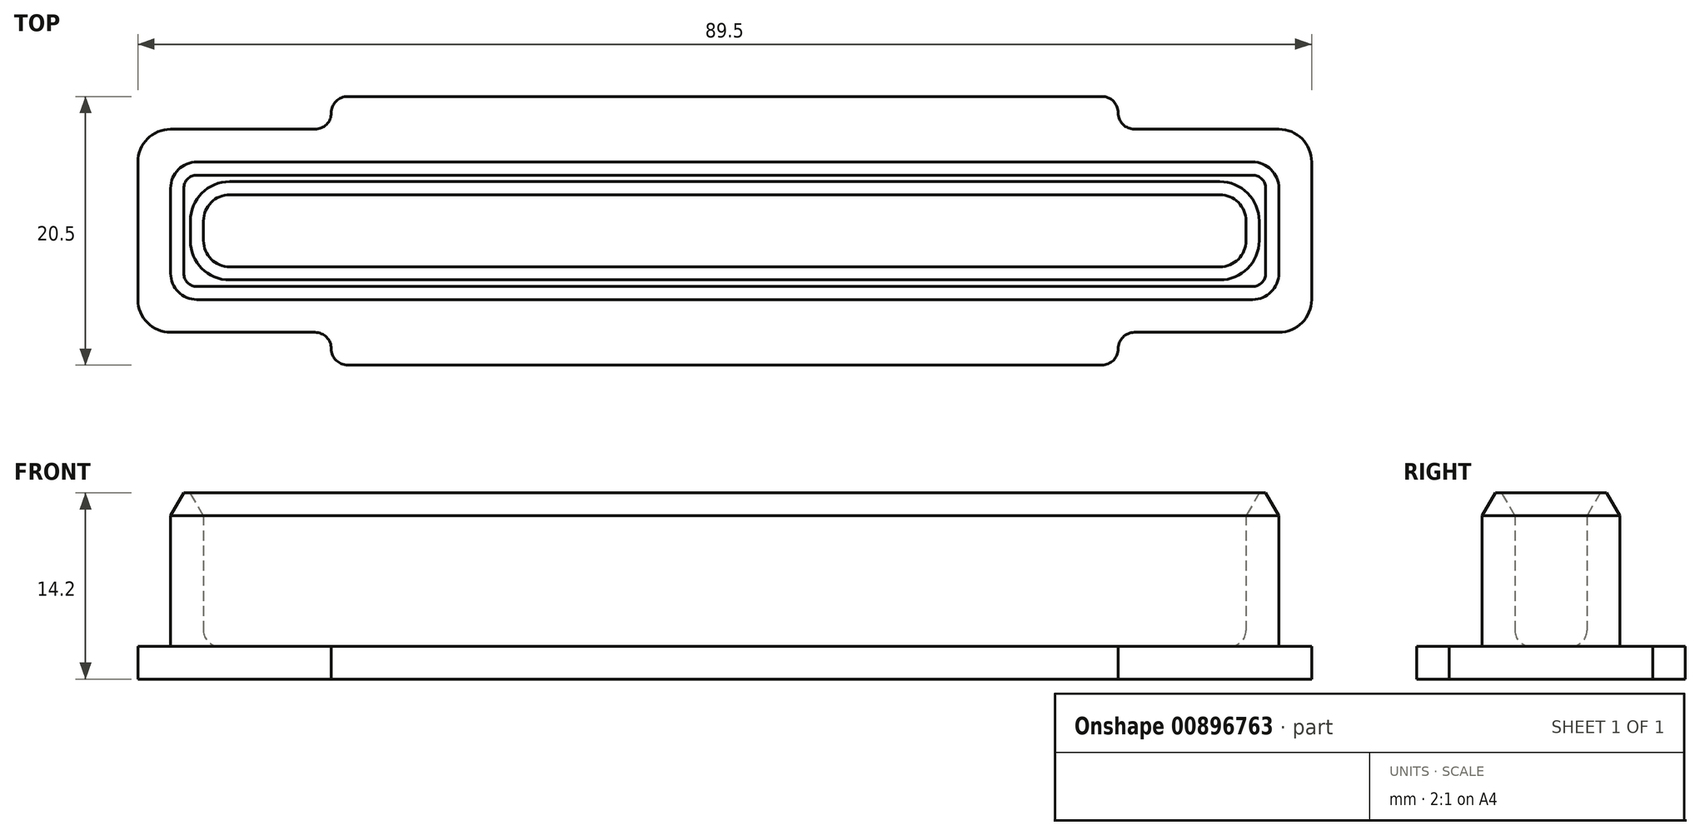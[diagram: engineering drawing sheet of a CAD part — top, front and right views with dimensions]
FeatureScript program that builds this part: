
annotation { "Feature Type Name" : "Feature", "Feature Type Description" : "" }
export const myFeature = defineFeature(function(context is Context, id is Id, definition is map)
    precondition{}
    {
        {
            var Q0;
            Q0=qCreatedBy(makeId("Top.planeOp"),FACE);
            var sketch = newSketch(context, id + "F0", { "sketchPlane" : qUnion([Q0])});
            skLineSegment(sketch, "E0.bottom", {"start": v(42.25, 5.25) * mm, "end": v(-42.25, 5.25) * mm});
            skLineSegment(sketch, "E0.top", {"start": v(42.25, -5.25) * mm, "end": v(-42.25, -5.25) * mm});
            skLineSegment(sketch, "E0.left", {"start": v(42.25, 5.25) * mm, "end": v(42.25, -5.25) * mm});
            skLineSegment(sketch, "E0.right", {"start": v(-42.25, 5.25) * mm, "end": v(-42.25, -5.25) * mm});
            skPoint(sketch, "E0.middle", {"position": v(0, 0) * mm});
            skLineSegment(sketch, "E1.bottom", {"start": v(44.75, 7.75) * mm, "end": v(-44.75, 7.75) * mm});
            skLineSegment(sketch, "E1.top", {"start": v(44.75, -7.75) * mm, "end": v(-44.75, -7.75) * mm});
            skLineSegment(sketch, "E1.left", {"start": v(44.75, 7.75) * mm, "end": v(44.75, -7.75) * mm});
            skLineSegment(sketch, "E1.right", {"start": v(-44.75, 7.75) * mm, "end": v(-44.75, -7.75) * mm});
            skLineSegment(sketch, "E2", {"start": v(0, 7.75) * mm, "end": v(0, 15.45) * mm, "construction": true});
            skLineSegment(sketch, "E3", {"start": v(0, 10.25) * mm, "end": v(30, 10.25) * mm});
            skLineSegment(sketch, "E4", {"start": v(30, 10.25) * mm, "end": v(30, 7.75) * mm});
            skLineSegment(sketch, "E5.MirrorCS", {"start": v(0, 10.25) * mm, "end": v(-30, 10.25) * mm});
            skLineSegment(sketch, "E6.MirrorCS", {"start": v(-30, 10.25) * mm, "end": v(-30, 7.75) * mm});
            skLineSegment(sketch, "E7.MirrorCS", {"start": v(0, -10.25) * mm, "end": v(30, -10.25) * mm});
            skLineSegment(sketch, "E8.MirrorCS", {"start": v(0, -10.25) * mm, "end": v(-30, -10.25) * mm});
            skLineSegment(sketch, "E9.MirrorCS", {"start": v(-30, -10.25) * mm, "end": v(-30, -7.75) * mm});
            skLineSegment(sketch, "E10.MirrorCS", {"start": v(30, -10.25) * mm, "end": v(30, -7.75) * mm});
            skSolve(sketch);
        }
        {
            var Q0;
            Q0=makeQuery(id+"F0.imprint","IMPRINT",FACE,{"disambiguationData":[TD([[makeQuery(id+"F0.imprint","IMPRINT",EDGE,{"derivedFrom":sQuery(id+"F0.wireOp",EDGE,"E0.bottom")}),1.0]])]});
            extrude(context, id + "F1", {"entities" : qUnion([Q0]), "depth" : 11.7 * mm, "offsetDistance" : 25 * mm});
        }
        {
            var Q0;
            Q0=makeQuery(id+"F1.opExtrude","CAP_FACE",FACE,{"disambiguationData":[OSD([sQuery(id+"F0.wireOp",EDGE,"E0.bottom"),sQuery(id+"F0.wireOp",EDGE,"E0.top"),sQuery(id+"F0.wireOp",EDGE,"E0.left"),sQuery(id+"F0.wireOp",EDGE,"E0.right")])],"isStart":false});
            var Q1;
            Q1=makeQuery(id+"F1.opExtrude","CAP_FACE",FACE,{"disambiguationData":[OSD([sQuery(id+"F0.wireOp",EDGE,"E0.bottom"),sQuery(id+"F0.wireOp",EDGE,"E0.top"),sQuery(id+"F0.wireOp",EDGE,"E0.left"),sQuery(id+"F0.wireOp",EDGE,"E0.right")])],"isStart":true});
            shell(context, id + "F2", {"entities" : qUnion([Q0, Q1]), "thickness" : 2.5 * mm});
        }
        {
            var Q0;
            Q0=makeQuery(id+"F0.imprint","IMPRINT",FACE,{"disambiguationData":[TD([[makeQuery(id+"F0.imprint","IMPRINT",EDGE,{"derivedFrom":sQuery(id+"F0.wireOp",EDGE,"E0.bottom")}),-1.0]])]});
            var Q1;
            Q1=makeQuery(id+"F0.imprint","IMPRINT",FACE,{"disambiguationData":[TD([[makeQuery(id+"F0.imprint","IMPRINT",EDGE,{"derivedFrom":sQuery(id+"F0.wireOp",EDGE,"E0.bottom")}),1.0]])]});
            extrude(context, id + "F3", {"entities" : qUnion([Q0, Q1]), "oppositeDirection" : true, "depth" : 2.5 * mm, "offsetDistance" : 25 * mm});
        }
        {
            var Q0;
            Q0=makeQuery(id+"F3.opExtrude","SWEPT_BODY",BODY,{"disambiguationData":[OSD([sQuery(id+"F0.wireOp",EDGE,"E1.bottom"),sQuery(id+"F0.wireOp",EDGE,"E1.top"),sQuery(id+"F0.wireOp",EDGE,"E1.left"),sQuery(id+"F0.wireOp",EDGE,"E1.right")])]});
            deleteBodies(context, id + "F4", {"entities" : qUnion([Q0])});
        }
        {
            var Q0;
            Q0=makeQuery(id+"F0.imprint","IMPRINT",FACE,{"disambiguationData":[TD([[makeQuery(id+"F0.imprint","IMPRINT",EDGE,{"derivedFrom":sQuery(id+"F0.wireOp",EDGE,"E3")}),-1.0]])]});
            var Q1;
            Q1=makeQuery(id+"F0.imprint","IMPRINT",FACE,{"disambiguationData":[TD([[makeQuery(id+"F0.imprint","IMPRINT",EDGE,{"derivedFrom":sQuery(id+"F0.wireOp",EDGE,"E0.bottom")}),-1.0]])]});
            var Q2;
            Q2=makeQuery(id+"F0.imprint","IMPRINT",FACE,{"disambiguationData":[TD([[makeQuery(id+"F0.imprint","IMPRINT",EDGE,{"derivedFrom":sQuery(id+"F0.wireOp",EDGE,"E7.MirrorCS")}),1.0]])]});
            var Q3;
            Q3=makeQuery(id+"F0.imprint","IMPRINT",FACE,{"disambiguationData":[TD([[makeQuery(id+"F0.imprint","IMPRINT",EDGE,{"derivedFrom":sQuery(id+"F0.wireOp",EDGE,"E0.bottom")}),1.0]])]});
            extrude(context, id + "F5", {"entities" : qUnion([Q0, Q1, Q2, Q3]), "operationType" : NewBodyOperationType.ADD, "oppositeDirection" : true, "depth" : 2.5 * mm, "offsetDistance" : 25 * mm});
        }
        {
            var Q0;
            {var subQ0=sQuery(id+"F0.wireOp",EDGE,"E0.bottom");Q0=makeQuery(id+"F2.opShell","OFFSET_EDGE",EDGE,{"disambiguationData":[OSD([subQ0]),TDD([makeQuery(id+"F1.opExtrude","CAP_EDGE",EDGE,{"disambiguationData":[OSD([subQ0])],"isStart":true})])]});}
            var Q1;
            {var subQ0=sQuery(id+"F0.wireOp",EDGE,"E0.left");Q1=makeQuery(id+"F2.opShell","OFFSET_EDGE",EDGE,{"disambiguationData":[OSD([subQ0]),TDD([makeQuery(id+"F1.opExtrude","CAP_EDGE",EDGE,{"disambiguationData":[OSD([subQ0])],"isStart":true})])]});}
            var Q2;
            {var subQ0=sQuery(id+"F0.wireOp",EDGE,"E0.top");Q2=makeQuery(id+"F2.opShell","OFFSET_EDGE",EDGE,{"disambiguationData":[OSD([subQ0]),TDD([makeQuery(id+"F1.opExtrude","CAP_EDGE",EDGE,{"disambiguationData":[OSD([subQ0])],"isStart":true})])]});}
            var Q3;
            {var subQ0=sQuery(id+"F0.wireOp",EDGE,"E0.right");Q3=makeQuery(id+"F2.opShell","OFFSET_EDGE",EDGE,{"disambiguationData":[OSD([subQ0]),TDD([makeQuery(id+"F1.opExtrude","CAP_EDGE",EDGE,{"disambiguationData":[OSD([subQ0])],"isStart":true})])]});}
            var Q4;
            Q4=makeQuery(id+"F1.opExtrude","CAP_EDGE",EDGE,{"disambiguationData":[OSD([sQuery(id+"F0.wireOp",EDGE,"E0.top")])],"isStart":true});
            var Q5;
            Q5=makeQuery(id+"F1.opExtrude","CAP_EDGE",EDGE,{"disambiguationData":[OSD([sQuery(id+"F0.wireOp",EDGE,"E0.right")])],"isStart":true});
            var Q6;
            Q6=makeQuery(id+"F1.opExtrude","CAP_EDGE",EDGE,{"disambiguationData":[OSD([sQuery(id+"F0.wireOp",EDGE,"E0.bottom")])],"isStart":true});
            var Q7;
            Q7=makeQuery(id+"F1.opExtrude","CAP_EDGE",EDGE,{"disambiguationData":[OSD([sQuery(id+"F0.wireOp",EDGE,"E0.left")])],"isStart":true});
            fillet(context, id + "F6", {"entities" : qUnion([Q0, Q1, Q2, Q3, Q4, Q5, Q6, Q7]), "radius" : 1.2 * mm, "tangentPropagation" : true, "allowEdgeOverflow" : false});
        }
        {
            var Q0;
            Q0=makeQuery(id+"F1.opExtrude","SWEPT_EDGE",EDGE,{"disambiguationData":[OSD([sQuery(id+"F0.wireOp",EDGE,"E0.bottom"),sQuery(id+"F0.wireOp",EDGE,"E0.left")])]});
            var Q1;
            Q1=makeQuery(id+"F1.opExtrude","SWEPT_EDGE",EDGE,{"disambiguationData":[OSD([sQuery(id+"F0.wireOp",EDGE,"E0.top"),sQuery(id+"F0.wireOp",EDGE,"E0.left")])]});
            var Q2;
            Q2=makeQuery(id+"F1.opExtrude","SWEPT_EDGE",EDGE,{"disambiguationData":[OSD([sQuery(id+"F0.wireOp",EDGE,"E0.top"),sQuery(id+"F0.wireOp",EDGE,"E0.right")])]});
            var Q3;
            Q3=makeQuery(id+"F1.opExtrude","SWEPT_EDGE",EDGE,{"disambiguationData":[OSD([sQuery(id+"F0.wireOp",EDGE,"E0.bottom"),sQuery(id+"F0.wireOp",EDGE,"E0.right")])]});
            var Q4;
            Q4=makeQuery(id+"F2.opShell","OFFSET_EDGE",EDGE,{"disambiguationData":[OSD([sQuery(id+"F0.wireOp",EDGE,"E0.top"),sQuery(id+"F0.wireOp",EDGE,"E0.left")])]});
            var Q5;
            Q5=makeQuery(id+"F2.opShell","OFFSET_EDGE",EDGE,{"disambiguationData":[OSD([sQuery(id+"F0.wireOp",EDGE,"E0.top"),sQuery(id+"F0.wireOp",EDGE,"E0.right")])]});
            var Q6;
            Q6=makeQuery(id+"F2.opShell","OFFSET_EDGE",EDGE,{"disambiguationData":[OSD([sQuery(id+"F0.wireOp",EDGE,"E0.bottom"),sQuery(id+"F0.wireOp",EDGE,"E0.right")])]});
            var Q7;
            Q7=makeQuery(id+"F2.opShell","OFFSET_EDGE",EDGE,{"disambiguationData":[OSD([sQuery(id+"F0.wireOp",EDGE,"E0.bottom"),sQuery(id+"F0.wireOp",EDGE,"E0.left")])]});
            fillet(context, id + "F7", {"entities" : qUnion([Q0, Q1, Q2, Q3, Q4, Q5, Q6, Q7]), "radius" : 2 * mm, "tangentPropagation" : true, "allowEdgeOverflow" : false});
        }
        {
            var Q0;
            Q0=makeQuery(id+"F5.opExtrude","SWEPT_EDGE",EDGE,{"disambiguationData":[OSD([sQuery(id+"F0.wireOp",EDGE,"E3"),sQuery(id+"F0.wireOp",EDGE,"E4")])]});
            var Q1;
            Q1=makeQuery(id+"F5.opExtrude","SWEPT_EDGE",EDGE,{"disambiguationData":[OSD([sQuery(id+"F0.wireOp",EDGE,"E1.bottom"),sQuery(id+"F0.wireOp",EDGE,"E4")])]});
            var Q2;
            Q2=makeQuery(id+"F5.opExtrude","SWEPT_EDGE",EDGE,{"disambiguationData":[OSD([sQuery(id+"F0.wireOp",EDGE,"E5.MirrorCS"),sQuery(id+"F0.wireOp",EDGE,"E6.MirrorCS")])]});
            var Q3;
            Q3=makeQuery(id+"F5.opExtrude","SWEPT_EDGE",EDGE,{"disambiguationData":[OSD([sQuery(id+"F0.wireOp",EDGE,"E1.bottom"),sQuery(id+"F0.wireOp",EDGE,"E6.MirrorCS")])]});
            var Q4;
            Q4=makeQuery(id+"F5.opExtrude","SWEPT_EDGE",EDGE,{"disambiguationData":[OSD([sQuery(id+"F0.wireOp",EDGE,"E1.top"),sQuery(id+"F0.wireOp",EDGE,"E9.MirrorCS")])]});
            var Q5;
            Q5=makeQuery(id+"F5.opExtrude","SWEPT_EDGE",EDGE,{"disambiguationData":[OSD([sQuery(id+"F0.wireOp",EDGE,"E8.MirrorCS"),sQuery(id+"F0.wireOp",EDGE,"E9.MirrorCS")])]});
            var Q6;
            Q6=makeQuery(id+"F5.opExtrude","SWEPT_EDGE",EDGE,{"disambiguationData":[OSD([sQuery(id+"F0.wireOp",EDGE,"E7.MirrorCS"),sQuery(id+"F0.wireOp",EDGE,"E10.MirrorCS")])]});
            var Q7;
            Q7=makeQuery(id+"F5.opExtrude","SWEPT_EDGE",EDGE,{"disambiguationData":[OSD([sQuery(id+"F0.wireOp",EDGE,"E1.top"),sQuery(id+"F0.wireOp",EDGE,"E10.MirrorCS")])]});
            fillet(context, id + "F8", {"entities" : qUnion([Q0, Q1, Q2, Q3, Q4, Q5, Q6, Q7]), "radius" : 1.25 * mm, "tangentPropagation" : true, "allowEdgeOverflow" : false});
        }
        {
            var Q0;
            Q0=makeQuery(id+"F5.opExtrude","SWEPT_EDGE",EDGE,{"disambiguationData":[OSD([sQuery(id+"F0.wireOp",EDGE,"E1.top"),sQuery(id+"F0.wireOp",EDGE,"E1.left")])]});
            var Q1;
            Q1=makeQuery(id+"F5.opExtrude","SWEPT_EDGE",EDGE,{"disambiguationData":[OSD([sQuery(id+"F0.wireOp",EDGE,"E1.bottom"),sQuery(id+"F0.wireOp",EDGE,"E1.left")])]});
            var Q2;
            Q2=makeQuery(id+"F5.opExtrude","SWEPT_EDGE",EDGE,{"disambiguationData":[OSD([sQuery(id+"F0.wireOp",EDGE,"E1.bottom"),sQuery(id+"F0.wireOp",EDGE,"E1.right")])]});
            var Q3;
            Q3=makeQuery(id+"F5.opExtrude","SWEPT_EDGE",EDGE,{"disambiguationData":[OSD([sQuery(id+"F0.wireOp",EDGE,"E1.top"),sQuery(id+"F0.wireOp",EDGE,"E1.right")])]});
            fillet(context, id + "F9", {"entities" : qUnion([Q0, Q1, Q2, Q3]), "radius" : 2.5 * mm, "tangentPropagation" : true, "allowEdgeOverflow" : false});
        }
        {
            var Q0;
            Q0=makeQuery(id+"F1.opExtrude","CAP_EDGE",EDGE,{"disambiguationData":[OSD([sQuery(id+"F0.wireOp",EDGE,"E0.bottom")])],"isStart":false});
            var Q1;
            {var subQ0=sQuery(id+"F0.wireOp",EDGE,"E0.bottom");Q1=makeQuery(id+"F2.opShell","OFFSET_EDGE",EDGE,{"disambiguationData":[OSD([subQ0]),TDD([makeQuery(id+"F1.opExtrude","CAP_EDGE",EDGE,{"disambiguationData":[OSD([subQ0])],"isStart":false})])]});}
            var Q2;
            {var subQ0=sQuery(id+"F0.wireOp",EDGE,"E0.top");Q2=makeQuery(id+"F2.opShell","OFFSET_EDGE",EDGE,{"disambiguationData":[OSD([subQ0]),TDD([makeQuery(id+"F1.opExtrude","CAP_EDGE",EDGE,{"disambiguationData":[OSD([subQ0])],"isStart":false})])]});}
            var Q3;
            Q3=makeQuery(id+"F1.opExtrude","CAP_EDGE",EDGE,{"disambiguationData":[OSD([sQuery(id+"F0.wireOp",EDGE,"E0.top")])],"isStart":false});
            var Q4;
            Q4=makeQuery(id+"F1.opExtrude","CAP_EDGE",EDGE,{"disambiguationData":[OSD([sQuery(id+"F0.wireOp",EDGE,"E0.left")])],"isStart":false});
            var Q5;
            Q5=makeQuery(id+"F1.opExtrude","CAP_EDGE",EDGE,{"disambiguationData":[OSD([sQuery(id+"F0.wireOp",EDGE,"E0.right")])],"isStart":false});
            chamfer(context, id + "F10", {"entities" : qUnion([Q0, Q1, Q2, Q3, Q4, Q5]), "chamferType" : ChamferType.OFFSET_ANGLE, "width" : 1 * mm, "oppositeDirection" : false, "angle" : 60 * degree, "tangentPropagation" : true});
        }
    });
